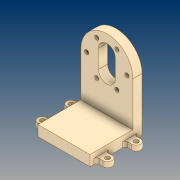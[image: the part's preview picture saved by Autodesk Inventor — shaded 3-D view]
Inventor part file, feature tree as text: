
AUTODESK INVENTOR PART (.ipt)
format: ipt  version: 2021 (Build 250183000, 183)  size: 227,840 bytes
history: native  units: mm
features: extrude x4, sketch x4, projected_geometry x3, fillet x2, plane x2, mirror x2
ambient origin geometry x8: Origin, YZ Plane, XZ Plane, XY Plane, X Axis, Y Axis, Z Axis, Center Point
bodies: Solid1 (feature_tree)
feature tree (17):
  extrude  "Extrusion1"  Depth=40.0mm
  extrude  "Extrusion2"  Depth=60.0mm TaperAngle=360.0deg
  extrude  "Extrusion3"  Depth=7.0mm
  fillet  "Fillet1"  Radius=7.0mm
  extrude  "Extrusion4"  Depth=2.0mm
  plane  "Work Plane1"
  plane  "Work Plane2"
  mirror  "Mirror2"
  mirror  "Mirror3"
  fillet  "Fillet4"  [1 undecoded]
  sketch  "Sketch1"  dims[d0=40.0mm d1=15.55mm]
  sketch  "Sketch2"  dims[d3=42.0mm d4=60.0mm d6=360.0deg]
  projected_geometry  "Projected Loop1"
  sketch  "Sketch3"  dims[d8=6.5mm d9=14.0mm d10=7.0mm d11=0.0mm]
  projected_geometry  "Projected Loop2"
  sketch  "Sketch4"  dims[d12=31.0mm d13=3.2mm d14=30.0deg d15=60.0mm d17=360.0deg d19=5.0mm d20=0.0mm d21=40.0mm d22=8.0mm d23=0.0mm d24=2.0mm d26=7.0mm d27=5.0mm d28=4.0mm d29=3.5mm d30=4.0mm d31=0.0mm d33=-2.0mm d34=2.0mm]
  projected_geometry  "Projected Loop3"
note: 1 required parameter value undecoded (feature->parameter linkage not recoverable at this tier; creation-order binding heuristic only, values carry confidence <= 0.55)
